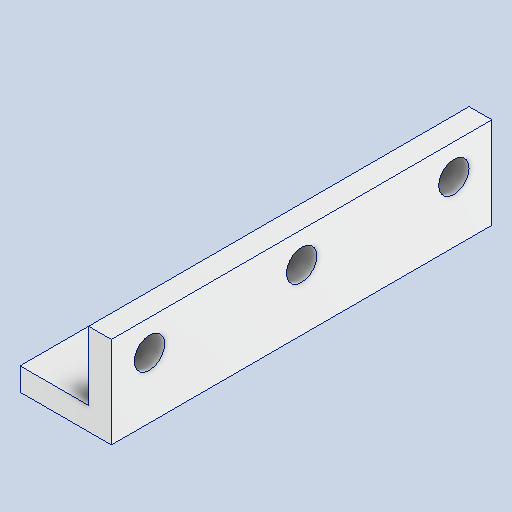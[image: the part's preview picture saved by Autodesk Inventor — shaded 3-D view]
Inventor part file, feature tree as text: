
AUTODESK INVENTOR PART (.ipt)
format: ipt  version: 2025.1 (Build 291241000, 241)  size: 113,664 bytes
history: native  units: mm
features: other x3, sketch x3
ambient origin geometry x8: Origin, YZ Plane, XZ Plane, XY Plane, X Axis, Y Axis, Z Axis, Center Point
bodies: Volumenkörper1 (feature_tree)
feature tree (6):
  other  "1172.ipt"
  other  "Volumenkörper1::1172.ipt"
  other  "TaggingFeature1"
  sketch  "Skizze1"  dims[d0=10.0mm]
  sketch  "Skizze2"
  sketch  "Skizze3"
